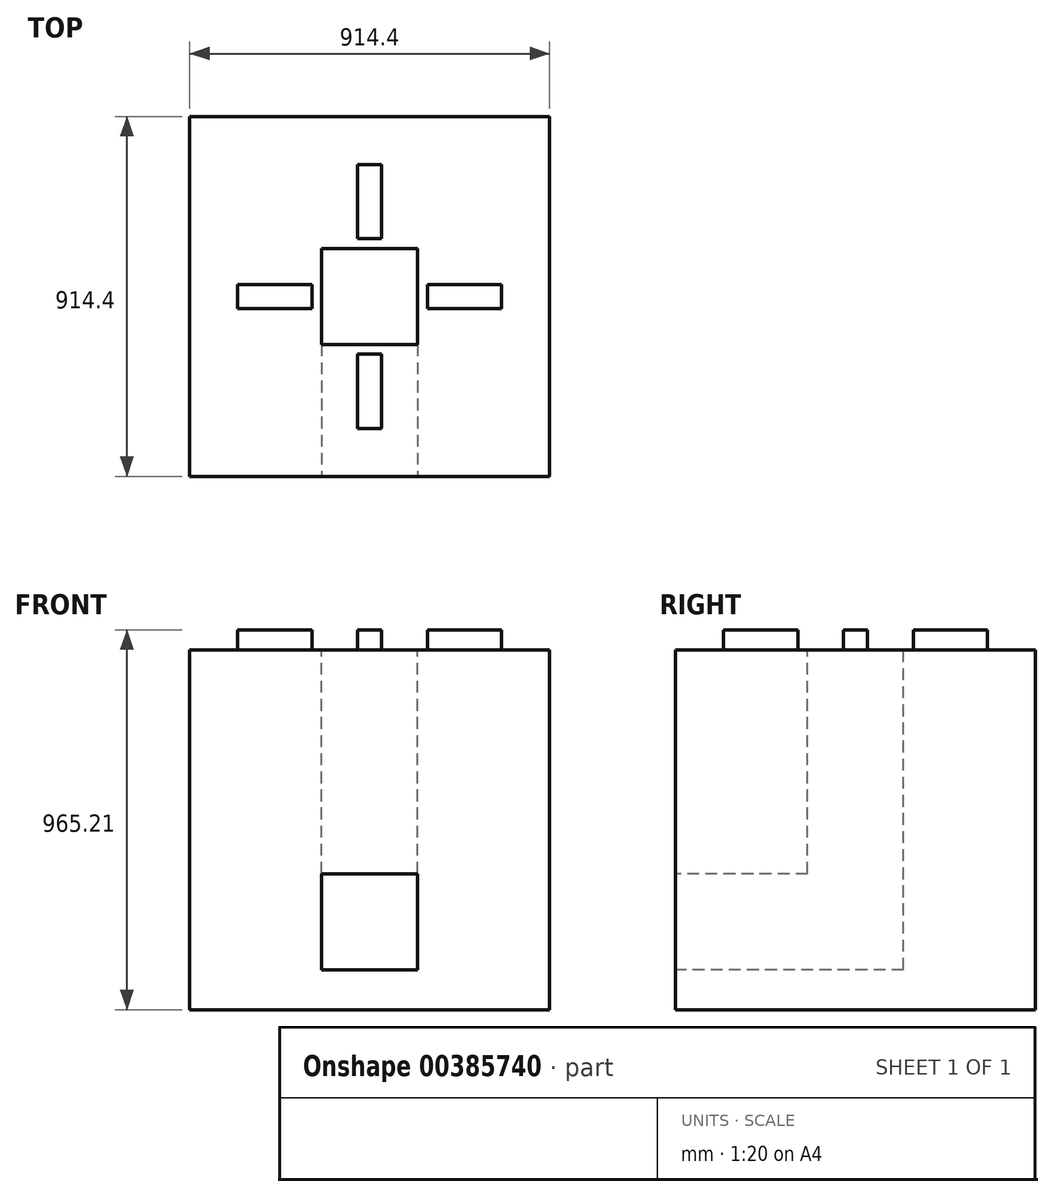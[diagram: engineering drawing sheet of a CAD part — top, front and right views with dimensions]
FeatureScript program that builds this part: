
annotation { "Feature Type Name" : "Feature", "Feature Type Description" : "" }
export const myFeature = defineFeature(function(context is Context, id is Id, definition is map)
    precondition{}
    {
        {
            var Q0;
            Q0=qCreatedBy(makeId("Front.planeOp"),FACE);
            var sketch = newSketch(context, id + "F0", { "sketchPlane" : qUnion([Q0])});
            skLineSegment(sketch, "E0.bottom", {"start": v(-457.2, -457.2) * mm, "end": v(457.2, -457.2) * mm});
            skLineSegment(sketch, "E0.top", {"start": v(-457.2, 457.2) * mm, "end": v(457.2, 457.2) * mm});
            skLineSegment(sketch, "E0.left", {"start": v(-457.2, -457.2) * mm, "end": v(-457.2, 457.2) * mm});
            skLineSegment(sketch, "E0.right", {"start": v(457.2, -457.2) * mm, "end": v(457.2, 457.2) * mm});
            skPoint(sketch, "E0.middle", {"position": v(0, 0) * mm});
            skPoint(sketch, "E1.middle.positionSnap0", {"position": v(0, -457.2) * mm});
            skPoint(sketch, "E1.centerSnap0", {"position": v(0, -457.2) * mm});
            skSolve(sketch);
        }
        {
            var Q0;
            Q0 = qSketchRegion(id + "F0", true);
            var Q1;
            Q1=makeQuery(id+"F0.imprint","IMPRINT",FACE,{"disambiguationData":[TD([[makeQuery(id+"F0.imprint","IMPRINT",EDGE,{"derivedFrom":sQuery(id+"F0.wireOp",EDGE,"E1.bottom")}),1.0]])]});
            extrude(context, id + "F1", {"entities" : qUnion([Q0, Q1]), "depth" : 914.4 * mm});
        }
        {
            var Q0;
            Q0=makeQuery(id+"F1.opExtrude","CAP_FACE",FACE,{"disambiguationData":[OSD([sQuery(id+"F0.wireOp",EDGE,"E0.bottom"),sQuery(id+"F0.wireOp",EDGE,"E0.top"),sQuery(id+"F0.wireOp",EDGE,"E0.left"),sQuery(id+"F0.wireOp",EDGE,"E0.right")])],"isStart":false});
            var sketch = newSketch(context, id + "F2", { "sketchPlane" : qUnion([Q0])});
            skLineSegment(sketch, "E2.bottom", {"start": v(121.92, -355.7) * mm, "end": v(-121.92, -355.7) * mm});
            skLineSegment(sketch, "E2.top", {"start": v(121.92, -111.86) * mm, "end": v(-121.92, -111.86) * mm});
            skLineSegment(sketch, "E2.left", {"start": v(121.92, -355.7) * mm, "end": v(121.92, -111.86) * mm});
            skLineSegment(sketch, "E2.right", {"start": v(-121.92, -355.7) * mm, "end": v(-121.92, -111.86) * mm});
            skPoint(sketch, "E2.middle", {"position": v(0, -233.78) * mm});
            skPoint(sketch, "E2.middle.positionSnap0", {"position": v(0, -457.2) * mm});
            skPoint(sketch, "E2.centerSnap0", {"position": v(0, -457.2) * mm});
            skSolve(sketch);
        }
        {
            var Q0;
            Q0 = qSketchRegion(id + "F2", true);
            extrude(context, id + "F3", {"entities" : qUnion([Q0]), "operationType" : NewBodyOperationType.REMOVE, "oppositeDirection" : true, "depth" : 335.28 * mm});
        }
        {
            var Q0;
            Q0=makeQuery(id+"F1.opExtrude","SWEPT_FACE",FACE,{"disambiguationData":[OSD([sQuery(id+"F0.wireOp",EDGE,"E0.top")])]});
            var sketch = newSketch(context, id + "F4", { "sketchPlane" : qUnion([Q0])});
            skLineSegment(sketch, "E3.bottom", {"start": v(-121.92, -579.12) * mm, "end": v(121.92, -579.12) * mm});
            skLineSegment(sketch, "E3.top", {"start": v(-121.92, -335.28) * mm, "end": v(121.92, -335.28) * mm});
            skLineSegment(sketch, "E3.left", {"start": v(-121.92, -579.12) * mm, "end": v(-121.92, -335.28) * mm});
            skLineSegment(sketch, "E3.right", {"start": v(121.92, -579.12) * mm, "end": v(121.92, -335.28) * mm});
            skPoint(sketch, "E3.middle", {"position": v(0, -457.2) * mm});
            skPoint(sketch, "E3.middle.positionSnap0", {"position": v(0, 0) * mm});
            skPoint(sketch, "E3.centerSnap0", {"position": v(0, 0) * mm});
            skSolve(sketch);
        }
        {
            var Q0;
            Q0 = qSketchRegion(id + "F4", true);
            extrude(context, id + "F5", {"entities" : qUnion([Q0]), "operationType" : NewBodyOperationType.REMOVE, "oppositeDirection" : true, "depth" : 812.9 * mm});
        }
        {
            var Q0;
            Q0=makeQuery(id+"F1.opExtrude","SWEPT_FACE",FACE,{"disambiguationData":[OSD([sQuery(id+"F0.wireOp",EDGE,"E0.top")])]});
            var sketch = newSketch(context, id + "F6", { "sketchPlane" : qUnion([Q0])});
            skLineSegment(sketch, "E4.bottom", {"start": v(335.28, -487.68) * mm, "end": v(146.6, -487.68) * mm});
            skLineSegment(sketch, "E4.top", {"start": v(335.28, -426.72) * mm, "end": v(146.6, -426.72) * mm});
            skLineSegment(sketch, "E4.left", {"start": v(335.28, -487.68) * mm, "end": v(335.28, -426.72) * mm});
            skLineSegment(sketch, "E4.right", {"start": v(146.6, -487.68) * mm, "end": v(146.6, -426.72) * mm});
            skPoint(sketch, "E4.middle", {"position": v(240.94, -457.2) * mm});
            skPoint(sketch, "E4.middle.positionSnap0", {"position": v(121.92, -457.2) * mm});
            skPoint(sketch, "E4.centerSnap0", {"position": v(121.92, -457.2) * mm});
            skLineSegment(sketch, "E5.bottom", {"start": v(-30.48, -121.92) * mm, "end": v(30.48, -121.92) * mm});
            skLineSegment(sketch, "E5.top", {"start": v(-30.48, -310.6) * mm, "end": v(30.48, -310.6) * mm});
            skLineSegment(sketch, "E5.left", {"start": v(-30.48, -121.92) * mm, "end": v(-30.48, -310.6) * mm});
            skLineSegment(sketch, "E5.right", {"start": v(30.48, -121.92) * mm, "end": v(30.48, -310.6) * mm});
            skPoint(sketch, "E5.middle", {"position": v(0, -216.26) * mm});
            skPoint(sketch, "E5.middle.positionSnap0", {"position": v(0, -335.28) * mm});
            skPoint(sketch, "E5.centerSnap0", {"position": v(0, -335.28) * mm});
            skLineSegment(sketch, "E6", {"start": v(0, 0) * mm, "end": v(0, -914.4) * mm, "construction": true});
            skLineSegment(sketch, "E7.MirrorCS", {"start": v(-335.28, -426.72) * mm, "end": v(-146.6, -426.72) * mm});
            skLineSegment(sketch, "E8.MirrorCS", {"start": v(-146.6, -487.68) * mm, "end": v(-146.6, -426.72) * mm});
            skLineSegment(sketch, "E9.MirrorCS", {"start": v(-335.28, -487.68) * mm, "end": v(-146.6, -487.68) * mm});
            skLineSegment(sketch, "E10.MirrorCS", {"start": v(-335.28, -487.68) * mm, "end": v(-335.28, -426.72) * mm});
            skLineSegment(sketch, "E11", {"start": v(-457.2, -457.2) * mm, "end": v(457.2, -457.2) * mm, "construction": true});
            skLineSegment(sketch, "E12.MirrorCS", {"start": v(-30.48, -792.48) * mm, "end": v(-30.48, -603.8) * mm});
            skLineSegment(sketch, "E13.MirrorCS", {"start": v(-30.48, -792.48) * mm, "end": v(30.48, -792.48) * mm});
            skLineSegment(sketch, "E14.MirrorCS", {"start": v(30.48, -792.48) * mm, "end": v(30.48, -603.8) * mm});
            skLineSegment(sketch, "E15.MirrorCS", {"start": v(-30.48, -603.8) * mm, "end": v(30.48, -603.8) * mm});
            skSolve(sketch);
        }
        {
            var Q0;
            Q0 = qSketchRegion(id + "F6", true);
            extrude(context, id + "F7", {"entities" : qUnion([Q0]), "operationType" : NewBodyOperationType.ADD, "depth" : 50.81 * mm, "hasSecondDirection" : true, "secondDirectionOppositeDirection" : true, "secondDirectionDepth" : 30.48 * mm});
        }
    });
